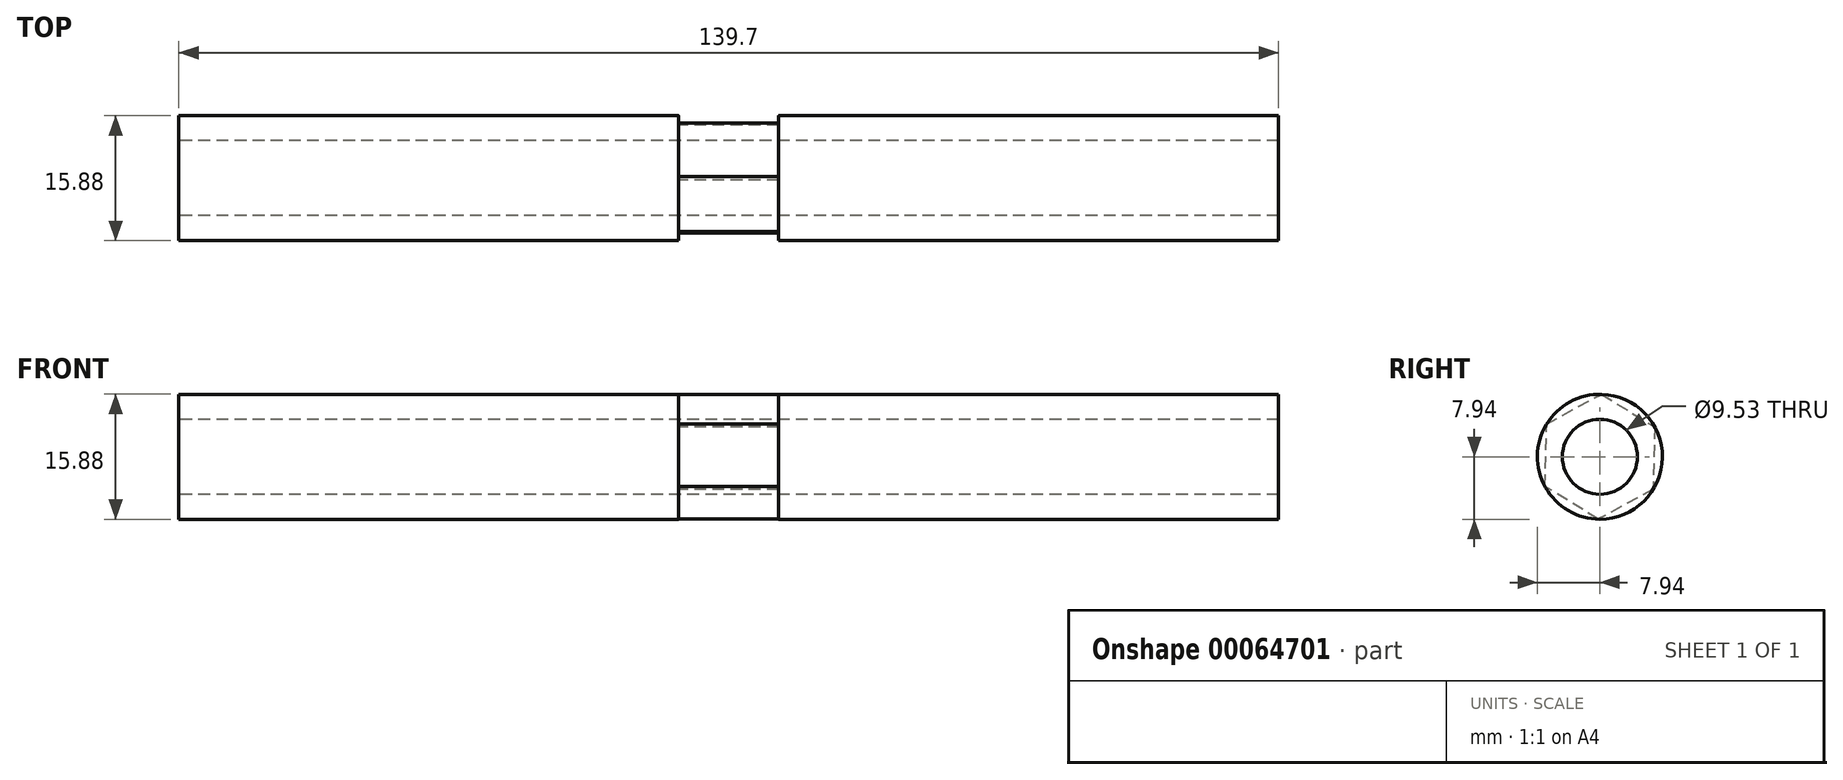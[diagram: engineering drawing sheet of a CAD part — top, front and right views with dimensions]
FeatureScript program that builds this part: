
annotation { "Feature Type Name" : "Feature", "Feature Type Description" : "" }
export const myFeature = defineFeature(function(context is Context, id is Id, definition is map)
    precondition{}
    {
        {
            var Q0;
            Q0=qCreatedBy(makeId("Right.planeOp"),FACE);
            var sketch = newSketch(context, id + "F0", { "sketchPlane" : qUnion([Q0])});
            skCircle(sketch, "E0", {"center": v(0, 0) * mm, "radius": 9.53 * mm});
            skCircle(sketch, "E1", {"center": v(0, 0) * mm, "radius": 15.88 * mm});
            skSolve(sketch);
        }
        {
            var Q0;
            Q0=makeQuery(id+"F0.imprint","IMPRINT",FACE,{"disambiguationData":[TD([[makeQuery(id+"F0.imprint","IMPRINT",EDGE,{"derivedFrom":sQuery(id+"F0.wireOp",EDGE,"E0")}),-1.0]])]});
            extrude(context, id + "F1", {"entities" : qUnion([Q0]), "depth" : 127 * mm});
        }
        {
            var Q0;
            Q0=makeQuery(id+"F1.opExtrude","CAP_FACE",FACE,{"disambiguationData":[OSD([sQuery(id+"F0.wireOp",EDGE,"E0"),sQuery(id+"F0.wireOp",EDGE,"E1")])],"isStart":false});
            var sketch = newSketch(context, id + "F2", { "sketchPlane" : qUnion([Q0])});
            skCircle(sketch, "E2.cCircle", {"center": v(0, 0) * mm, "radius": 15.88 * mm, "construction": true});
            skLineSegment(sketch, "E2.0", {"start": v(13.52, -8.33) * mm, "end": v(-0.45, -15.87) * mm});
            skLineSegment(sketch, "E2.1", {"start": v(-0.45, -15.87) * mm, "end": v(-13.97, -7.54) * mm});
            skLineSegment(sketch, "E2.2", {"start": v(-13.97, -7.54) * mm, "end": v(-13.52, 8.33) * mm});
            skLineSegment(sketch, "E2.3", {"start": v(-13.52, 8.33) * mm, "end": v(0.45, 15.87) * mm});
            skLineSegment(sketch, "E2.4", {"start": v(0.45, 15.87) * mm, "end": v(13.97, 7.54) * mm});
            skLineSegment(sketch, "E2.5", {"start": v(13.97, 7.54) * mm, "end": v(13.52, -8.33) * mm});
            skSolve(sketch);
        }
        {
            var Q0;
            Q0=makeQuery(id+"F2.imprint","IMPRINT",FACE,{"disambiguationData":[TD([[makeQuery(id+"F2.imprint","IMPRINT",EDGE,{"derivedFrom":sQuery(id+"F2.wireOp",EDGE,"E2.0")}),-1.0]])]});
            extrude(context, id + "F3", {"entities" : qUnion([Q0]), "operationType" : NewBodyOperationType.ADD, "depth" : 12.7 * mm});
        }
        {
            var Q0;
            Q0=makeQuery(id+"F1.opExtrude","SWEPT_BODY",BODY,{"disambiguationData":[OSD([sQuery(id+"F0.wireOp",EDGE,"E0"),sQuery(id+"F0.wireOp",EDGE,"E1")])]});
            var Q1;
            Q1=makeQuery(id+"F3.opExtrude","CAP_FACE",FACE,{"disambiguationData":[OSD([sQuery(id+"F0.wireOp",EDGE,"E0"),sQuery(id+"F2.wireOp",EDGE,"E2.0"),sQuery(id+"F2.wireOp",EDGE,"E2.1"),sQuery(id+"F2.wireOp",EDGE,"E2.2"),sQuery(id+"F2.wireOp",EDGE,"E2.3"),sQuery(id+"F2.wireOp",EDGE,"E2.4"),sQuery(id+"F2.wireOp",EDGE,"E2.5")])],"isStart":false});
            mirror(context, id + "F4", {"operationType" : NewBodyOperationType.ADD, "entities" : qUnion([Q0]), "mirrorPlane" : qUnion([Q1])});
        }
        {
            var Q0;
            Q0=makeQuery(id+"F1.opExtrude","SWEPT_BODY",BODY,{"disambiguationData":[OSD([sQuery(id+"F0.wireOp",EDGE,"E0"),sQuery(id+"F0.wireOp",EDGE,"E1")])]});
            var Q1;
            Q1=qCreatedBy(makeId("Origin.pointOp"),VERTEX);
            transform(context, id + "F5", {"entities" : qUnion([Q0]), "transformType" : TransformType.SCALE_UNIFORMLY, "scale" : .5, "scalePoint" : qUnion([Q1]), "makeCopy" : false});
        }
    });
